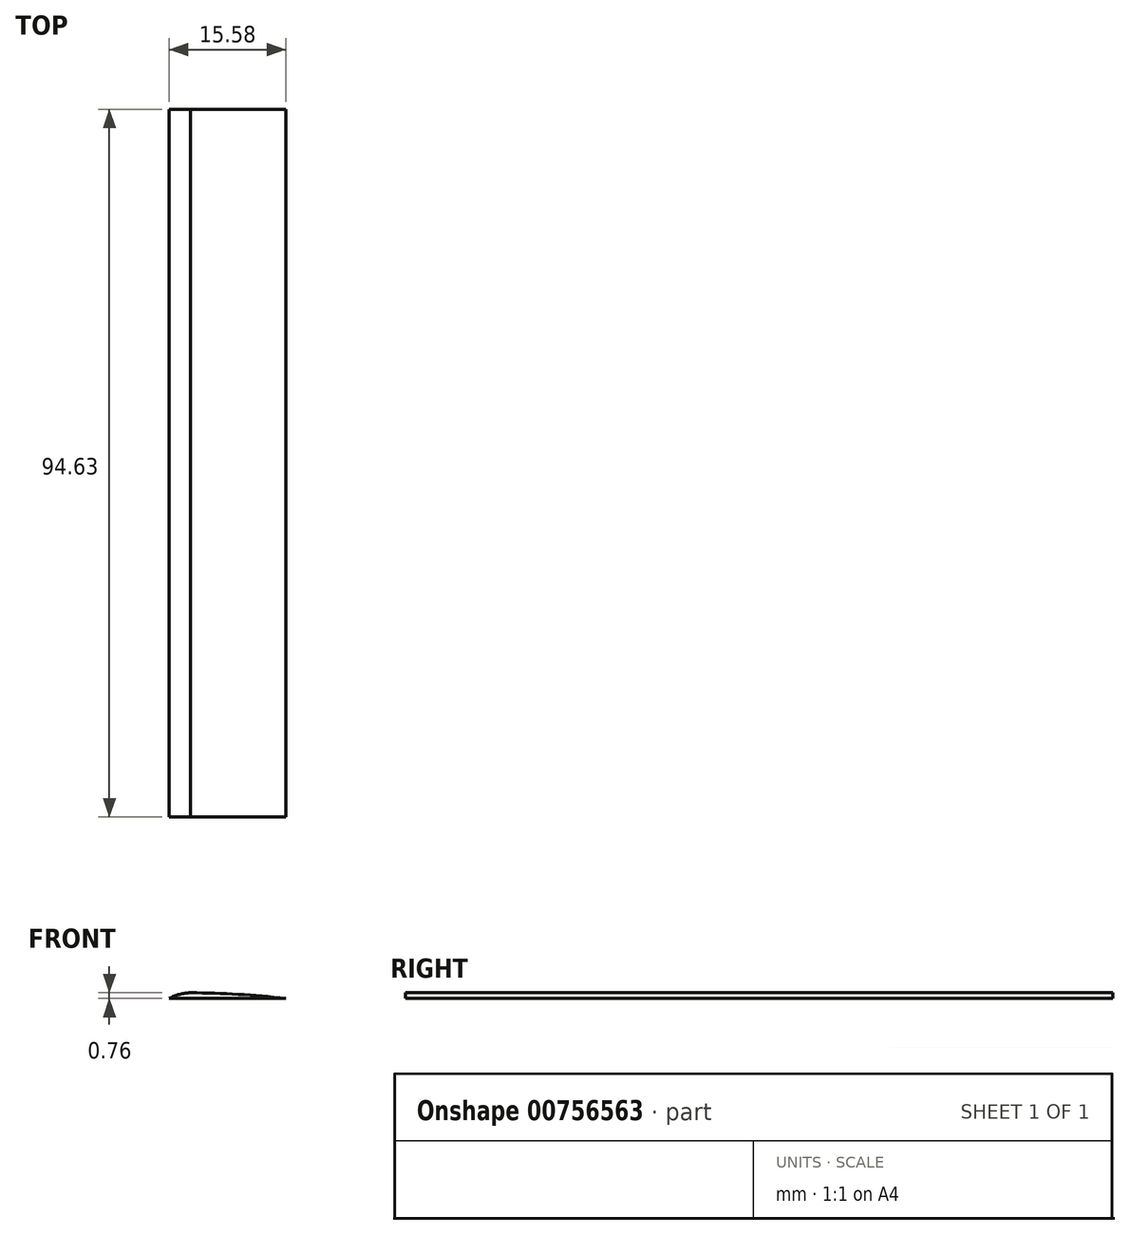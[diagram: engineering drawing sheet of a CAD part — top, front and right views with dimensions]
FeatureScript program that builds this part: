
annotation { "Feature Type Name" : "Feature", "Feature Type Description" : "" }
export const myFeature = defineFeature(function(context is Context, id is Id, definition is map)
    precondition{}
    {
        {
            var Q0;
            Q0=qCreatedBy(makeId("Top.planeOp"),FACE);
            var sketch = newSketch(context, id + "F0", { "sketchPlane" : qUnion([Q0])});
            skLineSegment(sketch, "E0.bottom", {"start": v(-49.6, 27.86) * mm, "end": v(-34.02, 27.86) * mm});
            skLineSegment(sketch, "E0.top", {"start": v(-49.6, -66.77) * mm, "end": v(-34.02, -66.77) * mm});
            skLineSegment(sketch, "E0.left", {"start": v(-49.6, 27.86) * mm, "end": v(-49.6, -66.77) * mm});
            skLineSegment(sketch, "E0.right", {"start": v(-34.02, 27.86) * mm, "end": v(-34.02, -66.77) * mm});
            skSolve(sketch);
        }
        {
            var Q0;
            Q0 = qSketchRegion(id + "F0", true);
            extrude(context, id + "F1", {"entities" : qUnion([Q0]), "depth" : 0.76 * mm, "offsetDistance" : 25.4 * mm});
        }
        {
            var Q0;
            Q0=makeQuery(id+"F1.opExtrude","CAP_EDGE",EDGE,{"disambiguationData":[OSD([sQuery(id+"F0.wireOp",EDGE,"E0.left")])],"isStart":false});
            fillet(context, id + "F2", {"entities" : qUnion([Q0]), "radius" : 6.13 * mm, "tangentPropagation" : true, "allowEdgeOverflow" : false});
        }
        {
            var Q0;
            Q0=makeQuery(id+"F1.opExtrude","CAP_EDGE",EDGE,{"disambiguationData":[OSD([sQuery(id+"F0.wireOp",EDGE,"E0.right")])],"isStart":false});
            fillet(context, id + "F3", {"entities" : qUnion([Q0]), "radius" : 114.67 * mm, "tangentPropagation" : true, "allowEdgeOverflow" : false});
        }
    });
